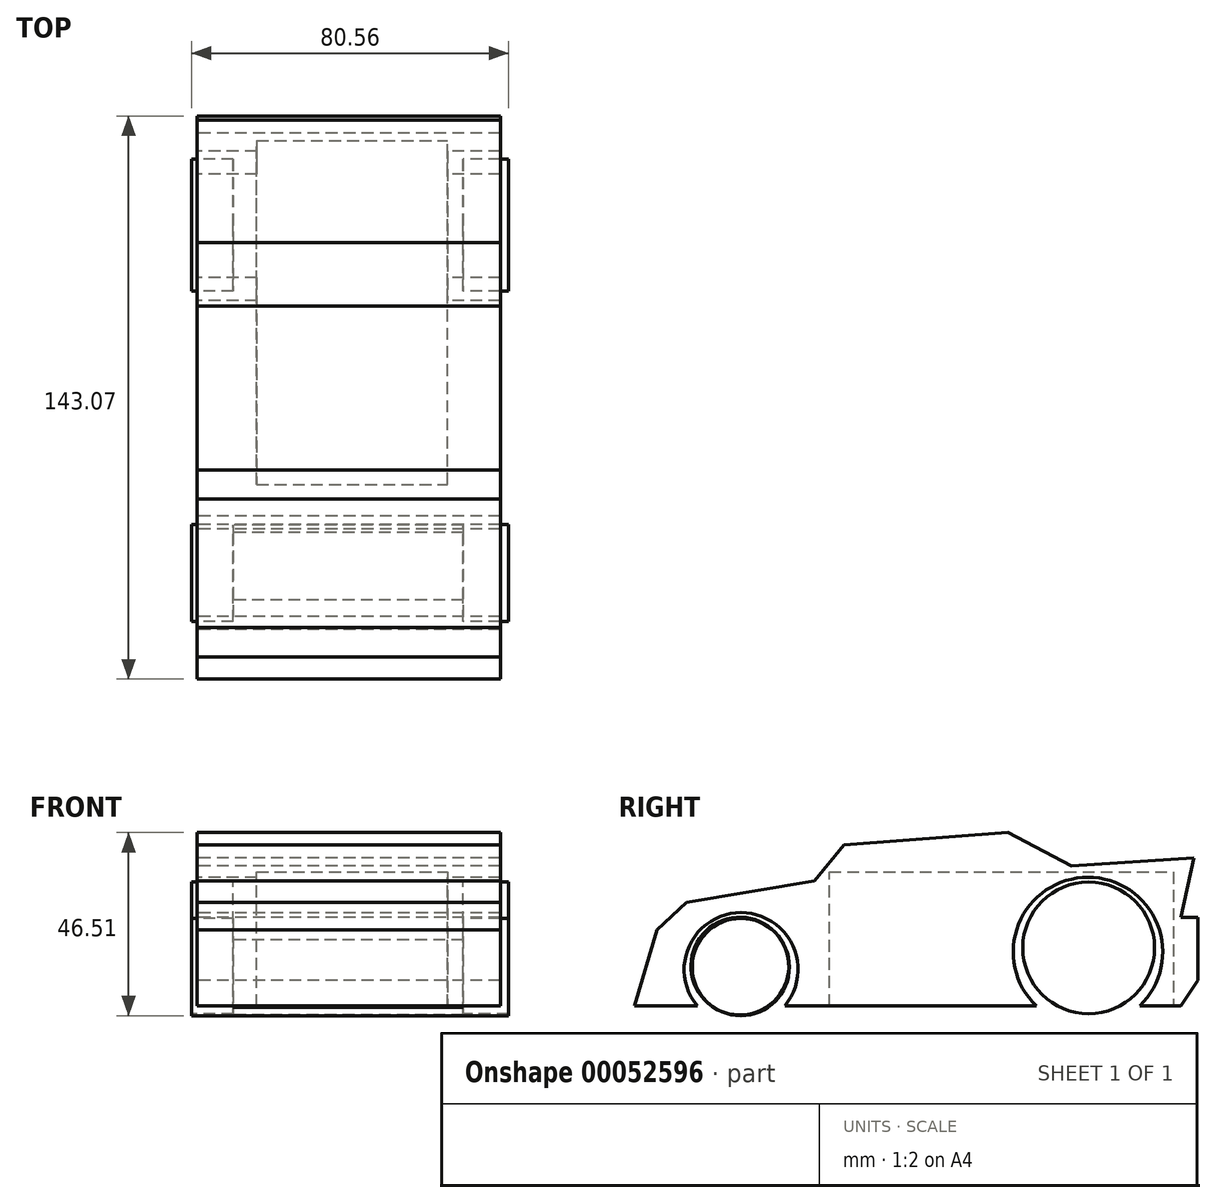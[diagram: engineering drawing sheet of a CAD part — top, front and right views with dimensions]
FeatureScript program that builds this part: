
annotation { "Feature Type Name" : "Feature", "Feature Type Description" : "" }
export const myFeature = defineFeature(function(context is Context, id is Id, definition is map)
    precondition{}
    {
        {
            var Q0;
            Q0=qCreatedBy(makeId("Right.planeOp"),FACE);
            var sketch = newSketch(context, id + "F0", { "sketchPlane" : qUnion([Q0])});
            skLineSegment(sketch, "E0", {"start": v(-73.72, 0) * mm, "end": v(64.98, 0) * mm});
            skLineSegment(sketch, "E1", {"start": v(64.98, 0) * mm, "end": v(69.35, 6.55) * mm});
            skLineSegment(sketch, "E2", {"start": v(69.35, 6.55) * mm, "end": v(69.35, 22.47) * mm});
            skLineSegment(sketch, "E3", {"start": v(69.35, 22.47) * mm, "end": v(64.98, 22.47) * mm});
            skLineSegment(sketch, "E4", {"start": v(64.98, 22.47) * mm, "end": v(68.32, 37.63) * mm});
            skLineSegment(sketch, "E5", {"start": v(68.32, 37.63) * mm, "end": v(37.24, 35.57) * mm});
            skLineSegment(sketch, "E6", {"start": v(37.24, 35.57) * mm, "end": v(21.06, 44.05) * mm});
            skLineSegment(sketch, "E7", {"start": v(21.06, 44.05) * mm, "end": v(-20.55, 40.97) * mm});
            skLineSegment(sketch, "E8", {"start": v(-20.55, 40.97) * mm, "end": v(-28, 31.72) * mm});
            skLineSegment(sketch, "E9", {"start": v(-28, 31.72) * mm, "end": v(-60.62, 26.33) * mm});
            skLineSegment(sketch, "E10", {"start": v(-60.62, 26.33) * mm, "end": v(-68.07, 19.4) * mm});
            skLineSegment(sketch, "E11", {"start": v(-68.07, 19.4) * mm, "end": v(-73.72, 0) * mm});
            skSolve(sketch);
        }
        {
            var Q0;
            Q0=makeQuery(id+"F0.imprint","IMPRINT",FACE,{"disambiguationData":[TD([[makeQuery(id+"F0.imprint","IMPRINT",EDGE,{"derivedFrom":sQuery(id+"F0.wireOp",EDGE,"E0")}),1.0]])]});
            extrude(context, id + "F1", {"entities" : qUnion([Q0]), "depth" : 47.52 * mm, "hasSecondDirection" : true, "secondDirectionOppositeDirection" : true, "secondDirectionDepth" : 29.45 * mm});
        }
        {
            var Q0;
            Q0=qCreatedBy(makeId("Right.planeOp"),FACE);
            var sketch = newSketch(context, id + "F2", { "sketchPlane" : qUnion([Q0])});
            skCircle(sketch, "E12", {"center": v(-46.7, 9.25) * mm, "radius": 14.46 * mm});
            skCircle(sketch, "E13", {"center": v(41.44, 13.71) * mm, "radius": 18.98 * mm});
            skSolve(sketch);
        }
        {
            var Q0;
            Q0 = qSketchRegion(id + "F2", true);
            extrude(context, id + "F3", {"entities" : qUnion([Q0]), "operationType" : NewBodyOperationType.REMOVE, "depth" : 83.4 * mm, "hasSecondDirection" : true, "secondDirectionOppositeDirection" : true, "secondDirectionDepth" : 94.24 * mm});
        }
        {
            var Q0;
            Q0=qCreatedBy(makeId("Right.planeOp"),FACE);
            var sketch = newSketch(context, id + "F4", { "sketchPlane" : qUnion([Q0])});
            skCircle(sketch, "E14", {"center": v(-46.75, 9.89) * mm, "radius": 12.35 * mm});
            skCircle(sketch, "E15", {"center": v(41.61, 14.77) * mm, "radius": 16.73 * mm});
            skSolve(sketch);
        }
        {
            var Q0;
            Q0=makeQuery(id+"F4.imprint","IMPRINT",FACE,{"disambiguationData":[TD([[makeQuery(id+"F4.imprint","IMPRINT",EDGE,{"derivedFrom":sQuery(id+"F4.wireOp",EDGE,"E14")}),1.0]])]});
            var Q1;
            Q1=makeQuery(id+"F4.imprint","IMPRINT",FACE,{"disambiguationData":[TD([[makeQuery(id+"F4.imprint","IMPRINT",EDGE,{"derivedFrom":sQuery(id+"F4.wireOp",EDGE,"E15")}),1.0]])]});
            extrude(context, id + "F5", {"entities" : qUnion([Q0, Q1]), "depth" : 49.66 * mm, "hasSecondDirection" : true, "secondDirectionOppositeDirection" : true, "secondDirectionDepth" : 30.9 * mm});
        }
        {
            var Q0;
            Q0=qCreatedBy(makeId("Right.planeOp"),FACE);
            var sketch = newSketch(context, id + "F6", { "sketchPlane" : qUnion([Q0])});
            skCircle(sketch, "E16", {"center": v(-47, 10.15) * mm, "radius": 12.42 * mm});
            skCircle(sketch, "E17", {"center": v(41.61, 14.51) * mm, "radius": 17.26 * mm});
            skSolve(sketch);
        }
        {
            var Q0;
            Q0 = qSketchRegion(id + "F6", true);
            extrude(context, id + "F7", {"entities" : qUnion([Q0]), "operationType" : NewBodyOperationType.REMOVE, "depth" : 38.1 * mm, "hasSecondDirection" : true, "secondDirectionOppositeDirection" : true, "secondDirectionDepth" : 20.32 * mm});
        }
        {
            var Q0;
            Q0=qCreatedBy(makeId("Front.planeOp"),FACE);
            var sketch = newSketch(context, id + "F8", { "sketchPlane" : qUnion([Q0])});
            skLineSegment(sketch, "E18", {"start": v(34.16, -2.95) * mm, "end": v(-14.38, -2.95) * mm});
            skLineSegment(sketch, "E19", {"start": v(-14.38, -2.95) * mm, "end": v(-14.38, 34.03) * mm});
            skLineSegment(sketch, "E20", {"start": v(-14.38, 34.03) * mm, "end": v(34.16, 34.03) * mm});
            skLineSegment(sketch, "E21", {"start": v(34.16, 34.03) * mm, "end": v(34.16, -2.95) * mm});
            skSolve(sketch);
        }
        {
            var Q0;
            Q0 = qSketchRegion(id + "F8", true);
            extrude(context, id + "F9", {"entities" : qUnion([Q0]), "operationType" : NewBodyOperationType.REMOVE, "depth" : 24.3 * mm, "hasSecondDirection" : true, "secondDirectionOppositeDirection" : true, "secondDirectionDepth" : 63.12 * mm});
        }
    });
